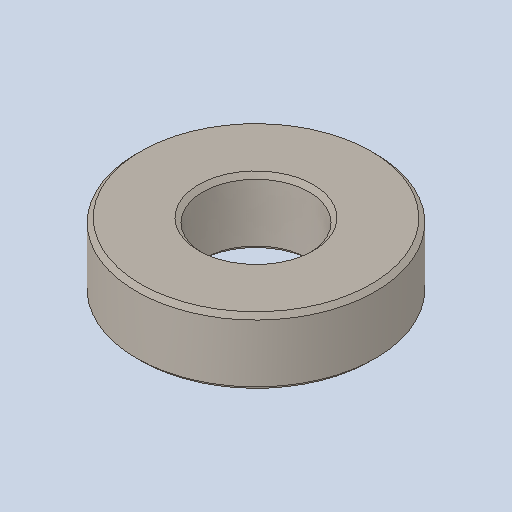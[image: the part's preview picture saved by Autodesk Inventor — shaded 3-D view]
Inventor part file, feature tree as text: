
AUTODESK INVENTOR PART (.ipt)
format: ipt  version: 2023 (Build 270158000, 158)  size: 101,888 bytes
history: native  units: in
note: dims shown in document units (in); Inventor stores cm internally (conversion verified against a paired STEP export)
features: chamfer x1
ambient origin geometry x8: Origin, YZ Plane, XZ Plane, XY Plane, X Axis, Y Axis, Z Axis, Center Point
bodies: Solid1 (feature_tree)
feature tree (1):
  chamfer  "Chamfer1"  [1 undecoded]
note: 1 required parameter value undecoded (feature->parameter linkage not recoverable at this tier; creation-order binding heuristic only, values carry confidence <= 0.55)
